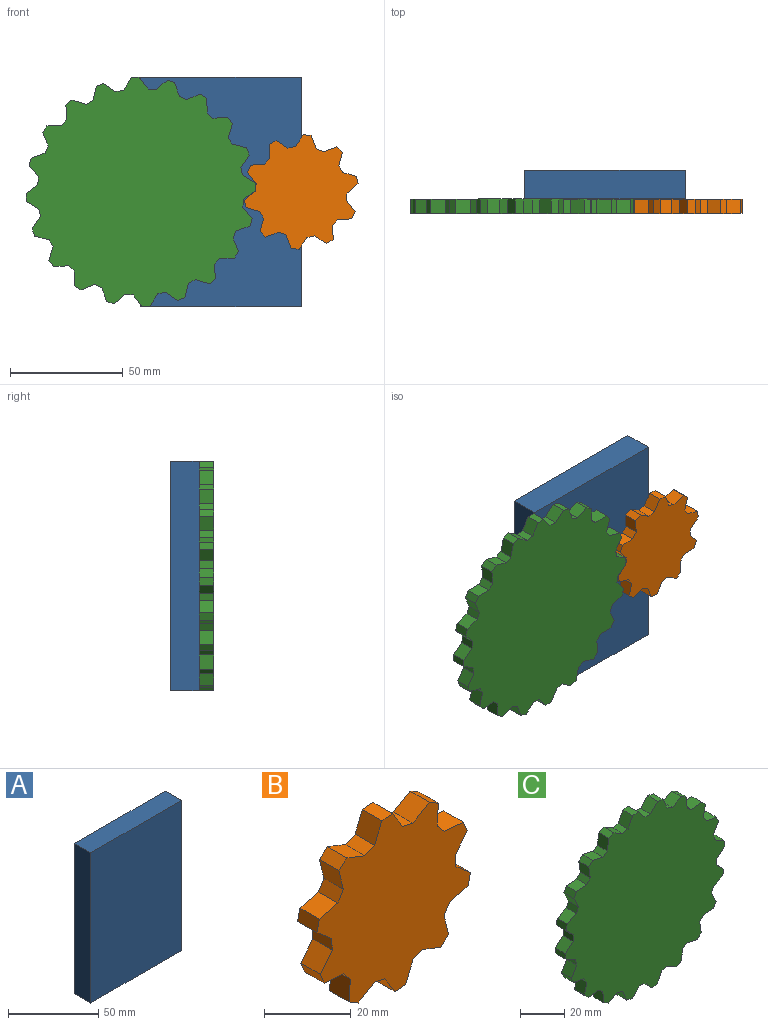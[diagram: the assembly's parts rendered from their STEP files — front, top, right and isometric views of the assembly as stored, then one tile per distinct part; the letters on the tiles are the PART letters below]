
ASSEMBLY  parts=3 mates=2
PART A: 6 faces, bbox 71.1x12.7x101.6 mm
  f0: plane 71.12x12.7mm, normal (0,0,1), area 903.2mm2, adj f1,f3,f4,f5
  f1: plane 101.6x12.7mm, normal (-1,0,0), area 1290.3mm2, adj f0,f2,f4,f5
  f2: plane 71.12x12.7mm, normal (0,0,-1), area 903.2mm2, adj f1,f3,f4,f5
  f3: plane 101.6x12.7mm, normal (1,0,0), area 1290.3mm2, adj f0,f2,f4,f5
  f4: plane 101.6x71.12mm, normal (0,-1,0), area 7225.8mm2, adj f0,f1,f2,f3
  f5: plane 101.6x71.12mm, normal (0,1,0), area 7225.8mm2, adj f0,f1,f2,f3
PART B: 42 faces, bbox 50.1x6.4x50.8 mm
  f0: plane 6.35x6.24mm, normal (0.08,0,1), area 39.7mm2, adj f3,f4,f5,f39
  f1: plane 6.35x3.44mm, normal (1,0,0.09), area 22mm2, adj f2,f4,f5,f6
  f2: plane 6.35x4.82mm, normal (0.77,0,-0.64), area 39.7mm2, adj f1,f3,f4,f5
  f3: plane 6.35x3.19mm, normal (0.92,0,0.39), area 22mm2, adj f0,f2,f4,f5
  f4: plane 50.79x50.14mm, normal (0,-1,0), area 1614.8mm2, adj f0,f1,f2,f3,f6,f7,f8,f9
  f5: plane 50.79x50.14mm, normal (0,1,0), area 1614.8mm2, adj f0,f1,f2,f3,f6,f7,f8,f9
  f6: plane 6.35x4.75mm, normal (0.65,0,0.76), area 39.7mm2, adj f1,f4,f5,f9
  f7: plane 6.35x2.96mm, normal (0.86,0,-0.52), area 22mm2, adj f4,f5,f8,f10
  f8: plane 6.35x6.06mm, normal (0.25,0,-0.97), area 39.7mm2, adj f4,f5,f7,f9
  f9: plane 6.35x3.37mm, normal (0.97,0,-0.23), area 22mm2, adj f4,f5,f6,f8
  f10: plane 6.35x6.09mm, normal (0.97,0,0.23), area 39.7mm2, adj f4,f5,f7,f13
  f11: plane 6.35x3.19mm, normal (0.39,0,-0.92), area 22mm2, adj f4,f5,f12,f14
  f12: plane 6.35x5.81mm, normal (-0.37,0,-0.93), area 39.7mm2, adj f4,f5,f11,f13
  f13: plane 6.35x2.61mm, normal (0.65,0,-0.76), area 22mm2, adj f4,f5,f10,f12
  f14: plane 6.35x5.78mm, normal (0.92,0,-0.38), area 39.7mm2, adj f4,f5,f11,f17
  f15: plane 6.35x3.37mm, normal (-0.23,0,-0.97), area 22mm2, adj f4,f5,f16,f18
  f16: plane 6.35x5.29mm, normal (-0.84,0,-0.53), area 39.7mm2, adj f4,f5,f15,f17
  f17: plane 6.35x3.44mm, normal (0.09,0,-1), area 22mm2, adj f4,f5,f14,f16
  f18: plane 6.35x5.34mm, normal (0.52,0,-0.85), area 39.7mm2, adj f4,f5,f15,f21
  f19: plane 6.35x2.61mm, normal (-0.76,0,-0.65), area 22mm2, adj f4,f5,f20,f22
  f20: plane 6.35x6.24mm, normal (-1,0,0.06), area 39.7mm2, adj f4,f5,f19,f21
  f21: plane 6.35x2.96mm, normal (-0.52,0,-0.86), area 22mm2, adj f4,f5,f18,f20
  f22: plane 6.35x6.24mm, normal (-0.08,0,-1), area 39.7mm2, adj f4,f5,f19,f25
  f23: plane 6.35x3.44mm, normal (-1,0,-0.09), area 22mm2, adj f4,f5,f24,f26
  f24: plane 6.35x4.82mm, normal (-0.77,0,0.64), area 39.7mm2, adj f4,f5,f23,f25
  f25: plane 6.35x3.19mm, normal (-0.92,0,-0.39), area 22mm2, adj f4,f5,f22,f24
  f26: plane 6.35x4.75mm, normal (-0.65,0,-0.76), area 39.7mm2, adj f4,f5,f23,f29
  f27: plane 6.35x2.96mm, normal (-0.86,0,0.52), area 22mm2, adj f4,f5,f28,f30
  f28: plane 6.35x6.06mm, normal (-0.25,0,0.97), area 39.7mm2, adj f4,f5,f27,f29
  f29: plane 6.35x3.37mm, normal (-0.97,0,0.23), area 22mm2, adj f4,f5,f26,f28
  f30: plane 6.35x6.09mm, normal (-0.97,0,-0.23), area 39.7mm2, adj f4,f5,f27,f33
  f31: plane 6.35x3.19mm, normal (-0.39,0,0.92), area 22mm2, adj f4,f5,f32,f34
  f32: plane 6.35x5.81mm, normal (0.37,0,0.93), area 39.7mm2, adj f4,f5,f31,f33
  f33: plane 6.35x2.61mm, normal (-0.65,0,0.76), area 22mm2, adj f4,f5,f30,f32
  f34: plane 6.35x5.78mm, normal (-0.92,0,0.38), area 39.7mm2, adj f4,f5,f31,f37
  f35: plane 6.35x3.37mm, normal (0.23,0,0.97), area 22mm2, adj f4,f5,f36,f38
  f36: plane 6.35x5.29mm, normal (0.84,0,0.53), area 39.7mm2, adj f4,f5,f35,f37
  f37: plane 6.35x3.44mm, normal (-0.09,0,1), area 22mm2, adj f4,f5,f34,f36
  f38: plane 6.35x5.34mm, normal (-0.52,0,0.85), area 39.7mm2, adj f4,f5,f35,f41
  f39: plane 6.35x2.61mm, normal (0.76,0,0.65), area 22mm2, adj f0,f4,f5,f40
  f40: plane 6.35x6.24mm, normal (1,0,-0.06), area 39.7mm2, adj f4,f5,f39,f41
  f41: plane 6.35x2.96mm, normal (0.52,0,0.86), area 22mm2, adj f4,f5,f38,f40
PART C: 82 faces, bbox 101.2x6.4x101.2 mm
  f0: plane 6.35x5.99mm, normal (-0.4,0,0.92), area 41.5mm2, adj f1,f4,f5,f81
  f1: plane 6.35x3.39mm, normal (-0.98,0,0.19), area 22mm2, adj f0,f2,f4,f5
  f2: plane 6.35x4.68mm, normal (-0.72,0,-0.7), area 41.5mm2, adj f1,f3,f4,f5
  f3: plane 6.35x3.45mm, normal (-1,0,0.04), area 22mm2, adj f2,f4,f5,f6
  f4: plane 101.23x101.23mm, normal (0,1,0), area 7288.9mm2, adj f0,f1,f2,f3,f6,f7,f8,f9
  f5: plane 101.23x101.23mm, normal (0,-1,0), area 7288.9mm2, adj f0,f1,f2,f3,f6,f7,f8,f9
  f6: plane 6.35x4.9mm, normal (-0.66,0,0.75), area 41.5mm2, adj f3,f4,f5,f7
  f7: plane 6.35x3.43mm, normal (-0.99,0,-0.12), area 22mm2, adj f4,f5,f6,f8
  f8: plane 6.35x5.78mm, normal (-0.47,0,-0.88), area 41.5mm2, adj f4,f5,f7,f9
  f9: plane 6.35x3.33mm, normal (-0.96,0,-0.27), area 22mm2, adj f4,f5,f8,f10
  f10: plane 6.35x5.63mm, normal (-0.86,0,0.51), area 41.5mm2, adj f4,f5,f9,f11
  f11: plane 6.35x3.14mm, normal (-0.91,0,-0.42), area 22mm2, adj f4,f5,f10,f12
  f12: plane 6.44x6.35mm, normal (-0.17,0,-0.99), area 41.5mm2, adj f4,f5,f11,f13
  f13: plane 6.35x2.87mm, normal (-0.83,0,-0.56), area 22mm2, adj f4,f5,f12,f14
  f14: plane 6.38x6.35mm, normal (-0.98,0,0.22), area 41.5mm2, adj f4,f5,f13,f15
  f15: plane 6.35x2.54mm, normal (-0.73,0,-0.68), area 22mm2, adj f4,f5,f14,f16
  f16: plane 6.47x6.35mm, normal (0.14,0,-0.99), area 41.5mm2, adj f4,f5,f15,f17
  f17: plane 6.35x2.72mm, normal (-0.62,0,-0.79), area 22mm2, adj f4,f5,f16,f18
  f18: plane 6.5x6.35mm, normal (-1,0,-0.1), area 41.5mm2, adj f4,f5,f17,f19
  f19: plane 6.35x3.02mm, normal (-0.49,0,-0.87), area 22mm2, adj f4,f5,f18,f20
  f20: plane 6.35x5.86mm, normal (0.44,0,-0.9), area 41.5mm2, adj f4,f5,f19,f21
  f21: plane 6.35x3.25mm, normal (-0.34,0,-0.94), area 22mm2, adj f4,f5,f20,f22
  f22: plane 6.35x5.99mm, normal (-0.92,0,-0.4), area 41.5mm2, adj f4,f5,f21,f23
  f23: plane 6.35x3.39mm, normal (-0.19,0,-0.98), area 22mm2, adj f4,f5,f22,f24
  f24: plane 6.35x4.68mm, normal (0.7,0,-0.72), area 41.5mm2, adj f4,f5,f23,f25
  f25: plane 6.35x3.45mm, normal (-0.04,0,-1), area 22mm2, adj f4,f5,f24,f26
  f26: plane 6.35x4.9mm, normal (-0.75,0,-0.66), area 41.5mm2, adj f4,f5,f25,f27
  f27: plane 6.35x3.43mm, normal (0.12,0,-0.99), area 22mm2, adj f4,f5,f26,f28
  f28: plane 6.35x5.78mm, normal (0.88,0,-0.47), area 41.5mm2, adj f4,f5,f27,f29
  f29: plane 6.35x3.33mm, normal (0.27,0,-0.96), area 22mm2, adj f4,f5,f28,f30
  f30: plane 6.35x5.63mm, normal (-0.51,0,-0.86), area 41.5mm2, adj f4,f5,f29,f31
  f31: plane 6.35x3.14mm, normal (0.42,0,-0.91), area 22mm2, adj f4,f5,f30,f32
  f32: plane 6.44x6.35mm, normal (0.99,0,-0.17), area 41.5mm2, adj f4,f5,f31,f33
  f33: plane 6.35x2.87mm, normal (0.56,0,-0.83), area 22mm2, adj f4,f5,f32,f34
  f34: plane 6.38x6.35mm, normal (-0.22,0,-0.98), area 41.5mm2, adj f4,f5,f33,f35
  f35: plane 6.35x2.54mm, normal (0.68,0,-0.73), area 22mm2, adj f4,f5,f34,f36
  f36: plane 6.47x6.35mm, normal (0.99,0,0.14), area 41.5mm2, adj f4,f5,f35,f37
  f37: plane 6.35x2.72mm, normal (0.79,0,-0.62), area 22mm2, adj f4,f5,f36,f38
  f38: plane 6.5x6.35mm, normal (0.1,0,-1), area 41.5mm2, adj f4,f5,f37,f39
  f39: plane 6.35x3.02mm, normal (0.87,0,-0.49), area 22mm2, adj f4,f5,f38,f40
  f40: plane 6.35x5.86mm, normal (0.9,0,0.44), area 41.5mm2, adj f4,f5,f39,f41
  f41: plane 6.35x3.25mm, normal (0.94,0,-0.34), area 22mm2, adj f4,f5,f40,f42
  f42: plane 6.35x5.99mm, normal (0.4,0,-0.92), area 41.5mm2, adj f4,f5,f41,f43
  f43: plane 6.35x3.39mm, normal (0.98,0,-0.19), area 22mm2, adj f4,f5,f42,f44
  f44: plane 6.35x4.68mm, normal (0.72,0,0.7), area 41.5mm2, adj f4,f5,f43,f45
  f45: plane 6.35x3.45mm, normal (1,0,-0.04), area 22mm2, adj f4,f5,f44,f46
  f46: plane 6.35x4.9mm, normal (0.66,0,-0.75), area 41.5mm2, adj f4,f5,f45,f47
  f47: plane 6.35x3.43mm, normal (0.99,0,0.12), area 22mm2, adj f4,f5,f46,f48
  f48: plane 6.35x5.78mm, normal (0.47,0,0.88), area 41.5mm2, adj f4,f5,f47,f49
  f49: plane 6.35x3.33mm, normal (0.96,0,0.27), area 22mm2, adj f4,f5,f48,f50
  f50: plane 6.35x5.63mm, normal (0.86,0,-0.51), area 41.5mm2, adj f4,f5,f49,f51
  f51: plane 6.35x3.14mm, normal (0.91,0,0.42), area 22mm2, adj f4,f5,f50,f52
  f52: plane 6.44x6.35mm, normal (0.17,0,0.99), area 41.5mm2, adj f4,f5,f51,f53
  f53: plane 6.35x2.87mm, normal (0.83,0,0.56), area 22mm2, adj f4,f5,f52,f54
  f54: plane 6.38x6.35mm, normal (0.98,0,-0.22), area 41.5mm2, adj f4,f5,f53,f55
  f55: plane 6.35x2.54mm, normal (0.73,0,0.68), area 22mm2, adj f4,f5,f54,f56
  f56: plane 6.47x6.35mm, normal (-0.14,0,0.99), area 41.5mm2, adj f4,f5,f55,f57
  f57: plane 6.35x2.72mm, normal (0.62,0,0.79), area 22mm2, adj f4,f5,f56,f58
  f58: plane 6.5x6.35mm, normal (1,0,0.1), area 41.5mm2, adj f4,f5,f57,f59
  f59: plane 6.35x3.02mm, normal (0.49,0,0.87), area 22mm2, adj f4,f5,f58,f60
  f60: plane 6.35x5.86mm, normal (-0.44,0,0.9), area 41.5mm2, adj f4,f5,f59,f61
  f61: plane 6.35x3.25mm, normal (0.34,0,0.94), area 22mm2, adj f4,f5,f60,f62
  f62: plane 6.35x5.99mm, normal (0.92,0,0.4), area 41.5mm2, adj f4,f5,f61,f63
  f63: plane 6.35x3.39mm, normal (0.19,0,0.98), area 22mm2, adj f4,f5,f62,f64
  f64: plane 6.35x4.68mm, normal (-0.7,0,0.72), area 41.5mm2, adj f4,f5,f63,f65
  f65: plane 6.35x3.45mm, normal (0.04,0,1), area 22mm2, adj f4,f5,f64,f66
  f66: plane 6.35x4.9mm, normal (0.75,0,0.66), area 41.5mm2, adj f4,f5,f65,f67
  f67: plane 6.35x3.43mm, normal (-0.12,0,0.99), area 22mm2, adj f4,f5,f66,f68
  f68: plane 6.35x5.78mm, normal (-0.88,0,0.47), area 41.5mm2, adj f4,f5,f67,f69
  f69: plane 6.35x3.33mm, normal (-0.27,0,0.96), area 22mm2, adj f4,f5,f68,f70
  f70: plane 6.35x5.63mm, normal (0.51,0,0.86), area 41.5mm2, adj f4,f5,f69,f71
  f71: plane 6.35x3.14mm, normal (-0.42,0,0.91), area 22mm2, adj f4,f5,f70,f72
  f72: plane 6.44x6.35mm, normal (-0.99,0,0.17), area 41.5mm2, adj f4,f5,f71,f73
  f73: plane 6.35x2.87mm, normal (-0.56,0,0.83), area 22mm2, adj f4,f5,f72,f74
  f74: plane 6.38x6.35mm, normal (0.22,0,0.98), area 41.5mm2, adj f4,f5,f73,f75
  f75: plane 6.35x2.54mm, normal (-0.68,0,0.73), area 22mm2, adj f4,f5,f74,f76
  f76: plane 6.47x6.35mm, normal (-0.99,0,-0.14), area 41.5mm2, adj f4,f5,f75,f77
  f77: plane 6.35x2.72mm, normal (-0.79,0,0.62), area 22mm2, adj f4,f5,f76,f78
  f78: plane 6.5x6.35mm, normal (-0.1,0,1), area 41.5mm2, adj f4,f5,f77,f79
  f79: plane 6.35x3.02mm, normal (-0.87,0,0.49), area 22mm2, adj f4,f5,f78,f80
  f80: plane 6.35x5.86mm, normal (-0.9,0,-0.44), area 41.5mm2, adj f4,f5,f79,f81
  f81: plane 6.35x3.25mm, normal (-0.94,0,0.34), area 22mm2, adj f0,f4,f5,f80
PLACE A t=(-134.36,6.35,-9.73)mm
PLACE B rot(axis=(-0.95,0,-0.3),180deg) t=(19.66,-12.7,-11.25)mm
PLACE C rot(axis=(0.97,0,0.24),180deg) t=(-51.46,-6.35,-11.25)mm
MATE revolute C.f5 <-> A.f4  axis (0,1,0) through (-51.46,-6.35,-11.25)mm
MATE revolute B.f4 <-> A.f4  axis (0,1,0) through (19.66,-6.35,-11.25)mm
